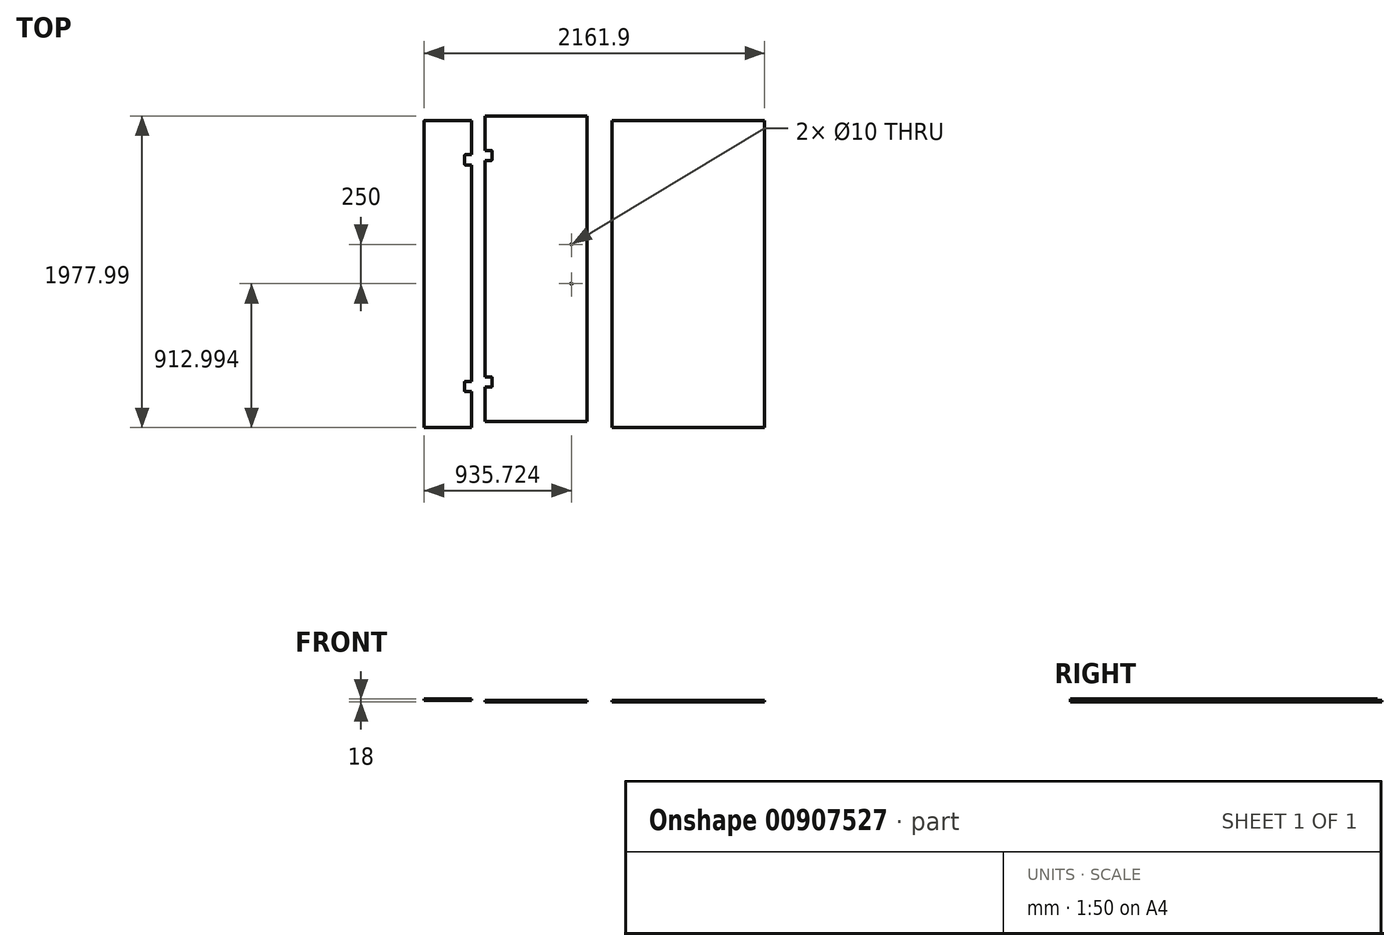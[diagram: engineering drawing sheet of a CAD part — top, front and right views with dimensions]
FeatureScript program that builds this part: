
annotation { "Feature Type Name" : "Feature", "Feature Type Description" : "" }
export const myFeature = defineFeature(function(context is Context, id is Id, definition is map)
    precondition{}
    {
        {
            var Q0;
            Q0=qCreatedBy(makeId("Top.planeOp"),FACE);
            var sketch = newSketch(context, id + "F0", { "sketchPlane" : qUnion([Q0])});
            skLineSegment(sketch, "E0.bottom", {"start": v(292.29, 0) * mm, "end": v(-7.71, 0) * mm});
            skLineSegment(sketch, "E0.top", {"start": v(292.29, 1950) * mm, "end": v(-2.71, 1950) * mm});
            skLineSegment(sketch, "E0.left", {"start": v(292.29, 0) * mm, "end": v(292.29, 1950) * mm});
            skLineSegment(sketch, "E0.right", {"start": v(-7.71, 0) * mm, "end": v(-7.71, 1945) * mm});
            skPoint(sketch, "E1.visualSharp", {"position": v(-7.71, 1950) * mm});
            skArc(sketch, "E1.filletArc", {"start": v(-2.71, 1950) * mm, "mid": v(-6.25, 1948.54) * mm, "end": v(-7.71, 1945) * mm});
            skSolve(sketch);
        }
        {
            var Q0;
            Q0=makeQuery(id+"F0.imprint","IMPRINT",FACE,{"disambiguationData":[TD([[makeQuery(id+"F0.imprint","IMPRINT",EDGE,{"derivedFrom":sQuery(id+"F0.wireOp",EDGE,"E0.bottom")}),-1.0]])]});
            extrude(context, id + "F1", {"entities" : qUnion([Q0]), "depth" : 8 * mm, "offsetDistance" : 25 * mm});
        }
        {
            var Q0;
            Q0=makeQuery(id+"F1.opExtrude","CAP_FACE",FACE,{"disambiguationData":[OSD([sQuery(id+"F0.wireOp",EDGE,"E0.bottom"),sQuery(id+"F0.wireOp",EDGE,"E0.top"),sQuery(id+"F0.wireOp",EDGE,"E0.left"),sQuery(id+"F0.wireOp",EDGE,"E0.right"),sQuery(id+"F0.wireOp",EDGE,"E1.filletArc")])],"isStart":false});
            var sketch = newSketch(context, id + "F2", { "sketchPlane" : qUnion([Q0])});
            skLineSegment(sketch, "E2.bottom", {"start": v(292.29, 1732) * mm, "end": v(253.29, 1732) * mm});
            skLineSegment(sketch, "E2.top", {"start": v(292.29, 1668) * mm, "end": v(253.29, 1668) * mm});
            skLineSegment(sketch, "E2.left", {"start": v(292.29, 1732) * mm, "end": v(292.29, 1668) * mm});
            skLineSegment(sketch, "E2.right", {"start": v(248.29, 1727) * mm, "end": v(248.29, 1673) * mm});
            skPoint(sketch, "E3.visualSharp", {"position": v(248.29, 1732) * mm});
            skArc(sketch, "E3.filletArc", {"start": v(253.29, 1732) * mm, "mid": v(249.75, 1730.54) * mm, "end": v(248.29, 1727) * mm});
            skPoint(sketch, "E4.visualSharp", {"position": v(248.29, 1668) * mm});
            skArc(sketch, "E4.filletArc", {"start": v(248.29, 1673) * mm, "mid": v(249.75, 1669.46) * mm, "end": v(253.29, 1668) * mm});
            skPoint(sketch, "E5", {"position": v(248.29, 1700) * mm});
            skLineSegment(sketch, "E6.bottom", {"start": v(292.29, 292) * mm, "end": v(253.29, 292) * mm});
            skLineSegment(sketch, "E6.top", {"start": v(292.29, 228) * mm, "end": v(253.29, 228) * mm});
            skLineSegment(sketch, "E6.left", {"start": v(292.29, 292) * mm, "end": v(292.29, 228) * mm});
            skLineSegment(sketch, "E6.right", {"start": v(248.29, 287) * mm, "end": v(248.29, 233) * mm});
            skPoint(sketch, "E7.visualSharp", {"position": v(248.29, 292) * mm});
            skArc(sketch, "E7.filletArc", {"start": v(253.29, 292) * mm, "mid": v(249.75, 290.54) * mm, "end": v(248.29, 287) * mm});
            skPoint(sketch, "E8.visualSharp", {"position": v(248.29, 228) * mm});
            skArc(sketch, "E8.filletArc", {"start": v(248.29, 233) * mm, "mid": v(249.75, 229.46) * mm, "end": v(253.29, 228) * mm});
            skPoint(sketch, "E9", {"position": v(248.29, 260) * mm});
            skSolve(sketch);
        }
        {
            var Q0;
            Q0=makeQuery(id+"F2.imprint","IMPRINT",FACE,{"disambiguationData":[TD([[makeQuery(id+"F2.imprint","IMPRINT",EDGE,{"derivedFrom":sQuery(id+"F2.wireOp",EDGE,"E2.bottom")}),1.0]])]});
            var Q1;
            Q1=makeQuery(id+"F2.imprint","IMPRINT",FACE,{"disambiguationData":[TD([[makeQuery(id+"F2.imprint","IMPRINT",EDGE,{"derivedFrom":sQuery(id+"F2.wireOp",EDGE,"E6.bottom")}),1.0]])]});
            extrude(context, id + "F3", {"entities" : qUnion([Q0, Q1]), "operationType" : NewBodyOperationType.REMOVE, "oppositeDirection" : true, "depth" : 25 * mm, "offsetDistance" : 25 * mm});
        }
        {
            var Q0;
            Q0=qCreatedBy(makeId("Top.planeOp"),FACE);
            var sketch = newSketch(context, id + "F4", { "sketchPlane" : qUnion([Q0])});
            skLineSegment(sketch, "E10.bottom", {"start": v(380.01, 1978) * mm, "end": v(1028.01, 1978) * mm});
            skLineSegment(sketch, "E10.top", {"start": v(380.01, 38) * mm, "end": v(1028.01, 38) * mm});
            skLineSegment(sketch, "E10.left", {"start": v(380.01, 1978) * mm, "end": v(380.01, 38) * mm});
            skLineSegment(sketch, "E10.right", {"start": v(1028.01, 1978) * mm, "end": v(1028.01, 38) * mm});
            skLineSegment(sketch, "E11.bottom", {"start": v(380.01, 1760) * mm, "end": v(419.01, 1760) * mm});
            skLineSegment(sketch, "E11.top", {"start": v(380.01, 1696) * mm, "end": v(419.01, 1696) * mm});
            skLineSegment(sketch, "E11.left", {"start": v(380.01, 1760) * mm, "end": v(380.01, 1696) * mm});
            skLineSegment(sketch, "E11.right", {"start": v(424.01, 1755) * mm, "end": v(424.01, 1701) * mm});
            skPoint(sketch, "E12.visualSharp", {"position": v(424.01, 1760) * mm});
            skArc(sketch, "E12.filletArc", {"start": v(424.01, 1755) * mm, "mid": v(422.55, 1758.53) * mm, "end": v(419.01, 1760) * mm});
            skPoint(sketch, "E13.visualSharp", {"position": v(424.01, 1696) * mm});
            skArc(sketch, "E13.filletArc", {"start": v(419.01, 1696) * mm, "mid": v(422.55, 1697.46) * mm, "end": v(424.01, 1701) * mm});
            skPoint(sketch, "E14", {"position": v(424.01, 1728) * mm});
            skLineSegment(sketch, "E15.bottom", {"start": v(380.01, 320) * mm, "end": v(419.01, 320) * mm});
            skLineSegment(sketch, "E15.top", {"start": v(380.01, 256) * mm, "end": v(419.01, 256) * mm});
            skLineSegment(sketch, "E15.left", {"start": v(380.01, 320) * mm, "end": v(380.01, 256) * mm});
            skLineSegment(sketch, "E15.right", {"start": v(424.01, 315) * mm, "end": v(424.01, 261) * mm});
            skPoint(sketch, "E16.visualSharp", {"position": v(424.01, 320) * mm});
            skArc(sketch, "E16.filletArc", {"start": v(424.01, 315) * mm, "mid": v(422.55, 318.53) * mm, "end": v(419.01, 320) * mm});
            skPoint(sketch, "E17.visualSharp", {"position": v(424.01, 256) * mm});
            skArc(sketch, "E17.filletArc", {"start": v(419.01, 256) * mm, "mid": v(422.55, 257.46) * mm, "end": v(424.01, 261) * mm});
            skPoint(sketch, "E18", {"position": v(424.01, 288) * mm});
            skSolve(sketch);
        }
        {
            var Q0;
            {var subQ6=sQuery(id+"F4.wireOp",EDGE,"E10.bottom");Q0=makeQuery(id+"F4.imprint","IMPRINT",FACE,{"disambiguationData":[TD([[makeQuery(id+"F4.imprint","IMPRINT",EDGE,{"derivedFrom":subQ6}),-1.0]])]});}
            extrude(context, id + "F5", {"entities" : qUnion([Q0]), "oppositeDirection" : true, "depth" : 10 * mm, "offsetDistance" : 25 * mm});
        }
        {
            var Q0;
            Q0=makeQuery(id+"F5.opExtrude","CAP_FACE",FACE,{"disambiguationData":[OSD([sQuery(id+"F4.wireOp",EDGE,"E10.bottom"),sQuery(id+"F4.wireOp",EDGE,"E10.top"),sQuery(id+"F4.wireOp",EDGE,"E10.left"),sQuery(id+"F4.wireOp",EDGE,"E10.right"),sQuery(id+"F4.wireOp",EDGE,"E11.bottom"),sQuery(id+"F4.wireOp",EDGE,"E11.top"),sQuery(id+"F4.wireOp",EDGE,"E11.right"),sQuery(id+"F4.wireOp",EDGE,"E12.filletArc"),sQuery(id+"F4.wireOp",EDGE,"E13.filletArc"),sQuery(id+"F4.wireOp",EDGE,"E15.bottom"),sQuery(id+"F4.wireOp",EDGE,"E15.top"),sQuery(id+"F4.wireOp",EDGE,"E15.right"),sQuery(id+"F4.wireOp",EDGE,"E16.filletArc"),sQuery(id+"F4.wireOp",EDGE,"E17.filletArc")])],"isStart":true});
            var sketch = newSketch(context, id + "F6", { "sketchPlane" : qUnion([Q0])});
            skCircle(sketch, "E19", {"center": v(928.01, 1163) * mm, "radius": 5 * mm});
            skCircle(sketch, "E20", {"center": v(928.01, 913) * mm, "radius": 5 * mm});
            skSolve(sketch);
        }
        {
            var Q0;
            Q0=makeQuery(id+"F6.imprint","IMPRINT",FACE,{"disambiguationData":[TD([[makeQuery(id+"F6.imprint","IMPRINT",EDGE,{"derivedFrom":sQuery(id+"F6.wireOp",EDGE,"E19")}),1.0]])]});
            var Q1;
            Q1=makeQuery(id+"F6.imprint","IMPRINT",FACE,{"disambiguationData":[TD([[makeQuery(id+"F6.imprint","IMPRINT",EDGE,{"derivedFrom":sQuery(id+"F6.wireOp",EDGE,"E20")}),1.0]])]});
            extrude(context, id + "F7", {"entities" : qUnion([Q0, Q1]), "operationType" : NewBodyOperationType.REMOVE, "endBound" : BoundingType.THROUGH_ALL, "oppositeDirection" : true, "depth" : 25 * mm, "offsetDistance" : 25 * mm});
        }
        {
            var Q0;
            Q0=qCreatedBy(makeId("Top.planeOp"),FACE);
            var sketch = newSketch(context, id + "F8", { "sketchPlane" : qUnion([Q0])});
            skLineSegment(sketch, "E21.bottom", {"start": v(1184.2, 0) * mm, "end": v(2154.2, 0) * mm});
            skLineSegment(sketch, "E21.top", {"start": v(1184.2, 1950) * mm, "end": v(2154.2, 1950) * mm});
            skLineSegment(sketch, "E21.left", {"start": v(1184.2, 0) * mm, "end": v(1184.2, 1950) * mm});
            skLineSegment(sketch, "E21.right", {"start": v(2154.2, 0) * mm, "end": v(2154.2, 1950) * mm});
            skSolve(sketch);
        }
        {
            var Q0;
            Q0=makeQuery(id+"F8.imprint","IMPRINT",FACE,{"disambiguationData":[TD([[makeQuery(id+"F8.imprint","IMPRINT",EDGE,{"derivedFrom":sQuery(id+"F8.wireOp",EDGE,"E21.bottom")}),1.0]])]});
            extrude(context, id + "F9", {"entities" : qUnion([Q0]), "oppositeDirection" : true, "depth" : 10 * mm, "offsetDistance" : 25 * mm});
        }
    });
